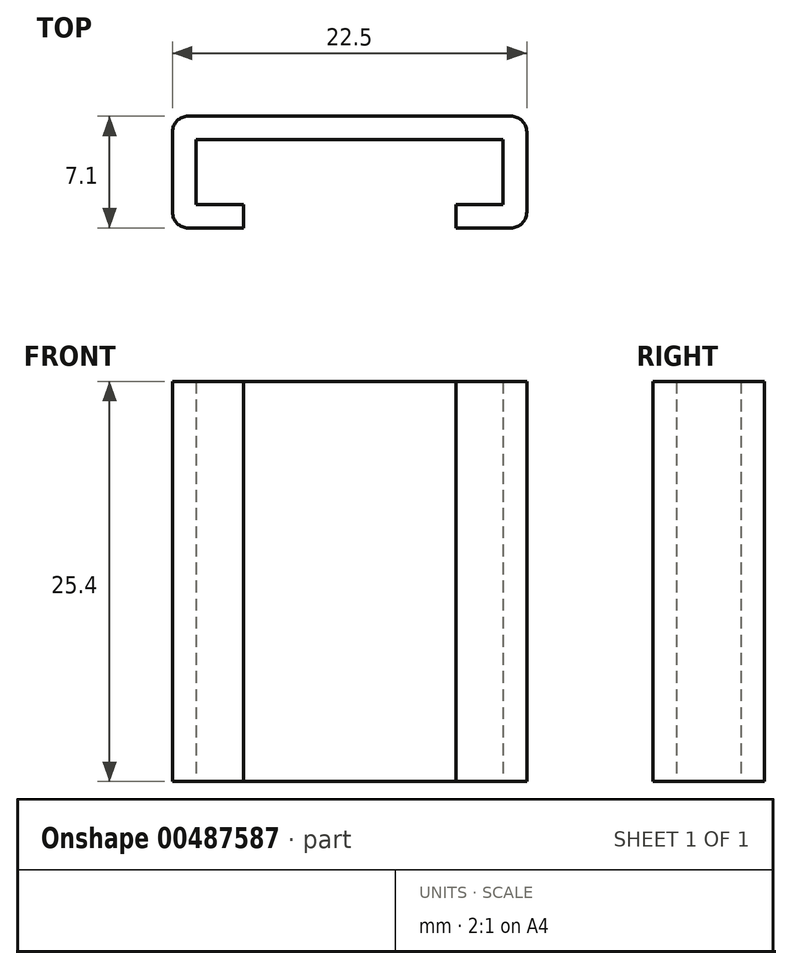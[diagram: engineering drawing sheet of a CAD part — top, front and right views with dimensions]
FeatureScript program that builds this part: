
annotation { "Feature Type Name" : "Feature", "Feature Type Description" : "" }
export const myFeature = defineFeature(function(context is Context, id is Id, definition is map)
    precondition{}
    {
        {
            var Q0;
            Q0=qCreatedBy(makeId("Top.planeOp"),FACE);
            var sketch = newSketch(context, id + "F0", { "sketchPlane" : qUnion([Q0])});
            skLineSegment(sketch, "E0", {"start": v(0, 0) * mm, "end": v(-9.75, 0) * mm});
            skLineSegment(sketch, "E1", {"start": v(-9.75, 0) * mm, "end": v(-9.75, -4.1) * mm});
            skLineSegment(sketch, "E2", {"start": v(-9.75, -4.1) * mm, "end": v(-6.75, -4.1) * mm});
            skLineSegment(sketch, "E3", {"start": v(0, 0) * mm, "end": v(0, 1.5) * mm});
            skLineSegment(sketch, "E4", {"start": v(0, 1.5) * mm, "end": v(-11.25, 1.5) * mm});
            skLineSegment(sketch, "E5", {"start": v(-11.25, 1.5) * mm, "end": v(-11.25, -5.6) * mm});
            skLineSegment(sketch, "E6", {"start": v(-11.25, -5.6) * mm, "end": v(-6.75, -5.6) * mm});
            skLineSegment(sketch, "E7", {"start": v(-6.75, -5.6) * mm, "end": v(-6.75, -4.1) * mm});
            skLineSegment(sketch, "E8.MirrorCS", {"start": v(11.25, 1.5) * mm, "end": v(11.25, -5.6) * mm});
            skLineSegment(sketch, "E9.MirrorCS", {"start": v(9.75, -4.1) * mm, "end": v(6.75, -4.1) * mm});
            skLineSegment(sketch, "E10.MirrorCS", {"start": v(0, 0) * mm, "end": v(9.75, 0) * mm});
            skLineSegment(sketch, "E11.MirrorCS", {"start": v(6.75, -5.6) * mm, "end": v(6.75, -4.1) * mm});
            skLineSegment(sketch, "E12.MirrorCS", {"start": v(0, 1.5) * mm, "end": v(11.25, 1.5) * mm});
            skLineSegment(sketch, "E13.MirrorCS", {"start": v(11.25, -5.6) * mm, "end": v(6.75, -5.6) * mm});
            skLineSegment(sketch, "E14.MirrorCS", {"start": v(9.75, 0) * mm, "end": v(9.75, -4.1) * mm});
            skSolve(sketch);
        }
        {
            var Q0;
            Q0 = qSketchRegion(id + "F0", true);
            extrude(context, id + "F1", {"entities" : qUnion([Q0]), "depth" : 25.4 * mm});
        }
        {
            var Q0;
            Q0=makeQuery(id+"F1.opExtrude","SWEPT_EDGE",EDGE,{"disambiguationData":[OSD([sQuery(id+"F0.wireOp",EDGE,"E4"),sQuery(id+"F0.wireOp",EDGE,"E5")])]});
            var Q1;
            Q1=makeQuery(id+"F1.opExtrude","SWEPT_EDGE",EDGE,{"disambiguationData":[OSD([sQuery(id+"F0.wireOp",EDGE,"E8.MirrorCS"),sQuery(id+"F0.wireOp",EDGE,"E12.MirrorCS")])]});
            fillet(context, id + "F2", {"entities" : qUnion([Q0, Q1]), "radius" : 1 * mm, "tangentPropagation" : true, "allowEdgeOverflow" : false});
        }
        {
            var Q0;
            Q0=makeQuery(id+"F1.opExtrude","SWEPT_EDGE",EDGE,{"disambiguationData":[OSD([sQuery(id+"F0.wireOp",EDGE,"E5"),sQuery(id+"F0.wireOp",EDGE,"E6")])]});
            var Q1;
            Q1=makeQuery(id+"F1.opExtrude","SWEPT_EDGE",EDGE,{"disambiguationData":[OSD([sQuery(id+"F0.wireOp",EDGE,"E8.MirrorCS"),sQuery(id+"F0.wireOp",EDGE,"E13.MirrorCS")])]});
            fillet(context, id + "F3", {"entities" : qUnion([Q0, Q1]), "radius" : 1 * mm, "tangentPropagation" : true, "allowEdgeOverflow" : false});
        }
    });
